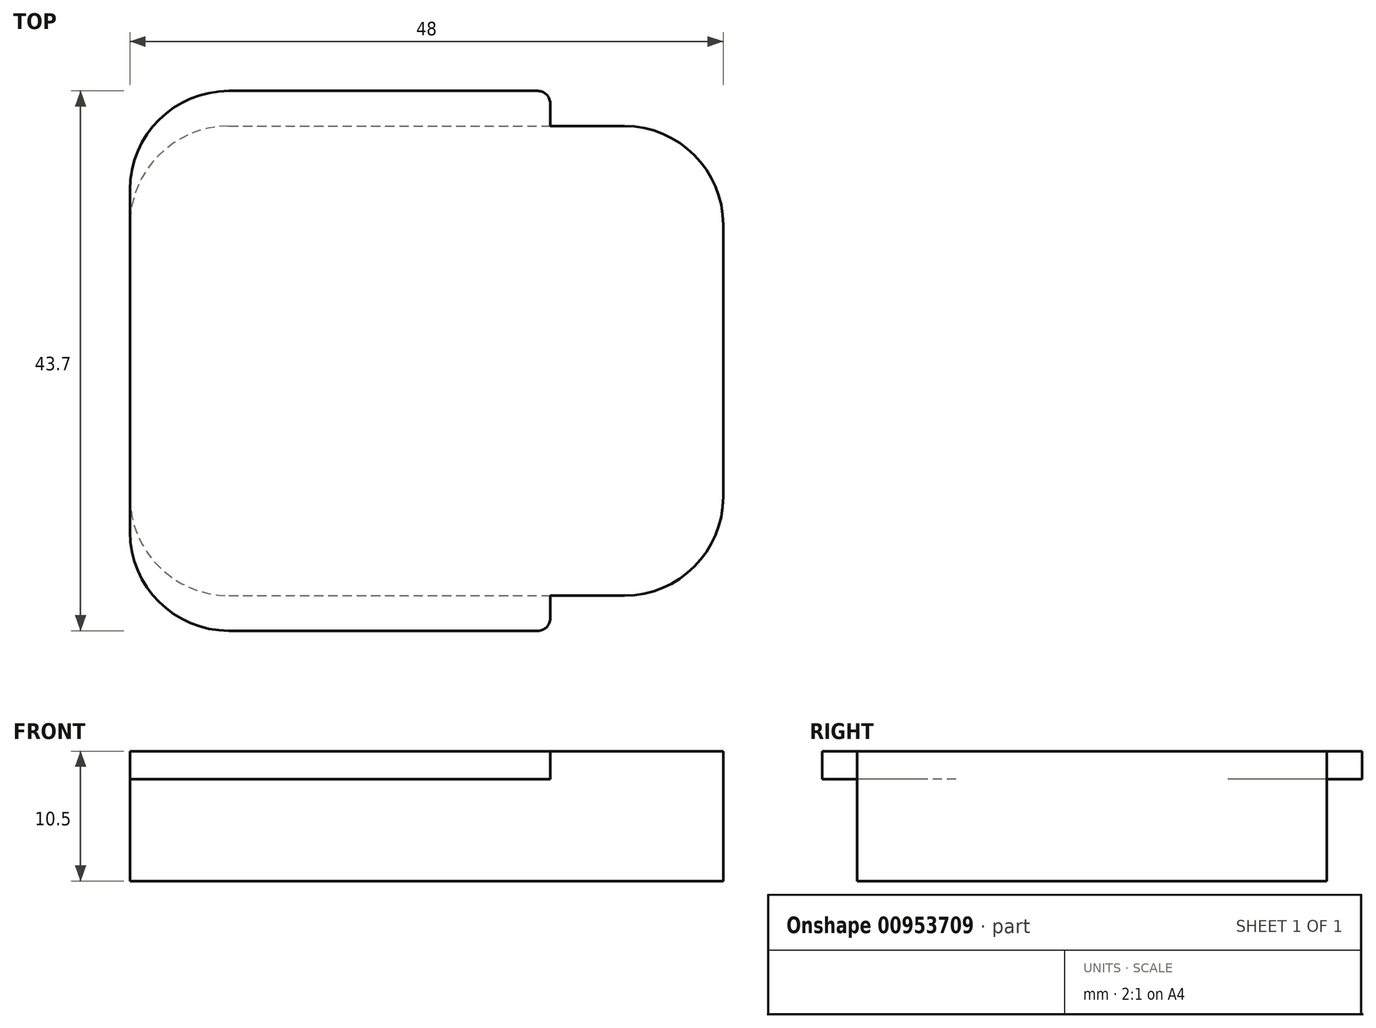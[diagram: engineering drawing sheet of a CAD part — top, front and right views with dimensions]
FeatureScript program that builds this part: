
annotation { "Feature Type Name" : "Feature", "Feature Type Description" : "" }
export const myFeature = defineFeature(function(context is Context, id is Id, definition is map)
    precondition{}
    {
        {
            var Q0;
            Q0=qCreatedBy(makeId("Top.planeOp"),FACE);
            var sketch = newSketch(context, id + "F0", { "sketchPlane" : qUnion([Q0])});
            skLineSegment(sketch, "E0.bottom", {"start": v(-16, 19) * mm, "end": v(16, 19) * mm});
            skLineSegment(sketch, "E0.top", {"start": v(-16, -19) * mm, "end": v(16, -19) * mm});
            skLineSegment(sketch, "E0.left", {"start": v(-24, 11) * mm, "end": v(-24, -11) * mm});
            skLineSegment(sketch, "E0.right", {"start": v(24, 11) * mm, "end": v(24, -11) * mm});
            skPoint(sketch, "E1.visualSharp", {"position": v(24, 19) * mm});
            skArc(sketch, "E1.filletArc", {"start": v(24, 11) * mm, "mid": v(21.66, 16.66) * mm, "end": v(16, 19) * mm});
            skPoint(sketch, "E2.visualSharp", {"position": v(24, -19) * mm});
            skArc(sketch, "E2.filletArc", {"start": v(16, -19) * mm, "mid": v(21.66, -16.66) * mm, "end": v(24, -11) * mm});
            skPoint(sketch, "E3.visualSharp", {"position": v(-24, -19) * mm});
            skArc(sketch, "E3.filletArc", {"start": v(-24, -11) * mm, "mid": v(-21.66, -16.66) * mm, "end": v(-16, -19) * mm});
            skPoint(sketch, "E4.visualSharp", {"position": v(-24, 19) * mm});
            skArc(sketch, "E4.filletArc", {"start": v(-16, 19) * mm, "mid": v(-21.66, 16.66) * mm, "end": v(-24, 11) * mm});
            skSolve(sketch);
        }
        {
            var Q0;
            Q0 = qSketchRegion(id + "F0", true);
            extrude(context, id + "F1", {"entities" : qUnion([Q0]), "depth" : 10.5 * mm, "offsetDistance" : 25 * mm});
        }
        {
            var Q0;
            Q0=makeQuery(id+"F1.opExtrude","CAP_FACE",FACE,{"disambiguationData":[OSD([sQuery(id+"F0.wireOp",EDGE,"E0.bottom"),sQuery(id+"F0.wireOp",EDGE,"E0.top"),sQuery(id+"F0.wireOp",EDGE,"E0.left"),sQuery(id+"F0.wireOp",EDGE,"E0.right"),sQuery(id+"F0.wireOp",EDGE,"E1.filletArc"),sQuery(id+"F0.wireOp",EDGE,"E2.filletArc"),sQuery(id+"F0.wireOp",EDGE,"E3.filletArc"),sQuery(id+"F0.wireOp",EDGE,"E4.filletArc")])],"isStart":false});
            var sketch = newSketch(context, id + "F2", { "sketchPlane" : qUnion([Q0])});
            skLineSegment(sketch, "E5.bottom", {"start": v(-16, 21.85) * mm, "end": v(10, 21.85) * mm});
            skLineSegment(sketch, "E5.top", {"start": v(-16, -21.85) * mm, "end": v(10, -21.85) * mm});
            skLineSegment(sketch, "E5.left", {"start": v(-24, 13.85) * mm, "end": v(-24, -13.85) * mm});
            skLineSegment(sketch, "E5.right", {"start": v(10, 21.85) * mm, "end": v(10, -21.85) * mm});
            skPoint(sketch, "E6.visualSharp", {"position": v(-24, 21.85) * mm});
            skArc(sketch, "E6.filletArc", {"start": v(-16, 21.85) * mm, "mid": v(-21.66, 19.5) * mm, "end": v(-24, 13.85) * mm});
            skPoint(sketch, "E7.visualSharp", {"position": v(-24, -21.85) * mm});
            skArc(sketch, "E7.filletArc", {"start": v(-24, -13.85) * mm, "mid": v(-21.66, -19.5) * mm, "end": v(-16, -21.85) * mm});
            skSolve(sketch);
        }
        {
            var Q0;
            {var subQ4=sQuery(id+"F2.wireOp",EDGE,"E5.bottom");Q0=makeQuery(id+"F2.imprint","IMPRINT",FACE,{"disambiguationData":[TD([[makeQuery(id+"F2.imprint","IMPRINT",EDGE,{"derivedFrom":subQ4}),-1.0]])]});}
            var Q1;
            {var subQ1=sQuery(id+"F2.wireOp",EDGE,"E5.top");Q1=makeQuery(id+"F2.imprint","IMPRINT",FACE,{"disambiguationData":[TD([[makeQuery(id+"F2.imprint","IMPRINT",EDGE,{"derivedFrom":subQ1}),1.0]])]});}
            extrude(context, id + "F3", {"entities" : qUnion([Q0, Q1]), "operationType" : NewBodyOperationType.ADD, "oppositeDirection" : true, "depth" : 2.25 * mm, "offsetDistance" : 25 * mm});
        }
        {
            var Q0;
            Q0=makeQuery(id+"F3.opExtrude","SWEPT_EDGE",EDGE,{"disambiguationData":[OSD([sQuery(id+"F0.wireOp",EDGE,"E0.top"),sQuery(id+"F2.wireOp",EDGE,"E5.right")])]});
            var Q1;
            Q1=makeQuery(id+"F3.opExtrude","SWEPT_EDGE",EDGE,{"disambiguationData":[OSD([sQuery(id+"F2.wireOp",EDGE,"E5.top"),sQuery(id+"F2.wireOp",EDGE,"E5.right")])]});
            var Q2;
            Q2=makeQuery(id+"F3.opExtrude","SWEPT_EDGE",EDGE,{"disambiguationData":[OSD([sQuery(id+"F2.wireOp",EDGE,"E5.bottom"),sQuery(id+"F2.wireOp",EDGE,"E5.right")])]});
            var Q3;
            Q3=makeQuery(id+"F3.opExtrude","SWEPT_EDGE",EDGE,{"disambiguationData":[OSD([sQuery(id+"F0.wireOp",EDGE,"E0.bottom"),sQuery(id+"F2.wireOp",EDGE,"E5.right")])]});
            fillet(context, id + "F4", {"entities" : qUnion([Q0, Q1, Q2, Q3]), "radius" : 1 * mm, "tangentPropagation" : true, "allowEdgeOverflow" : false});
        }
    });
